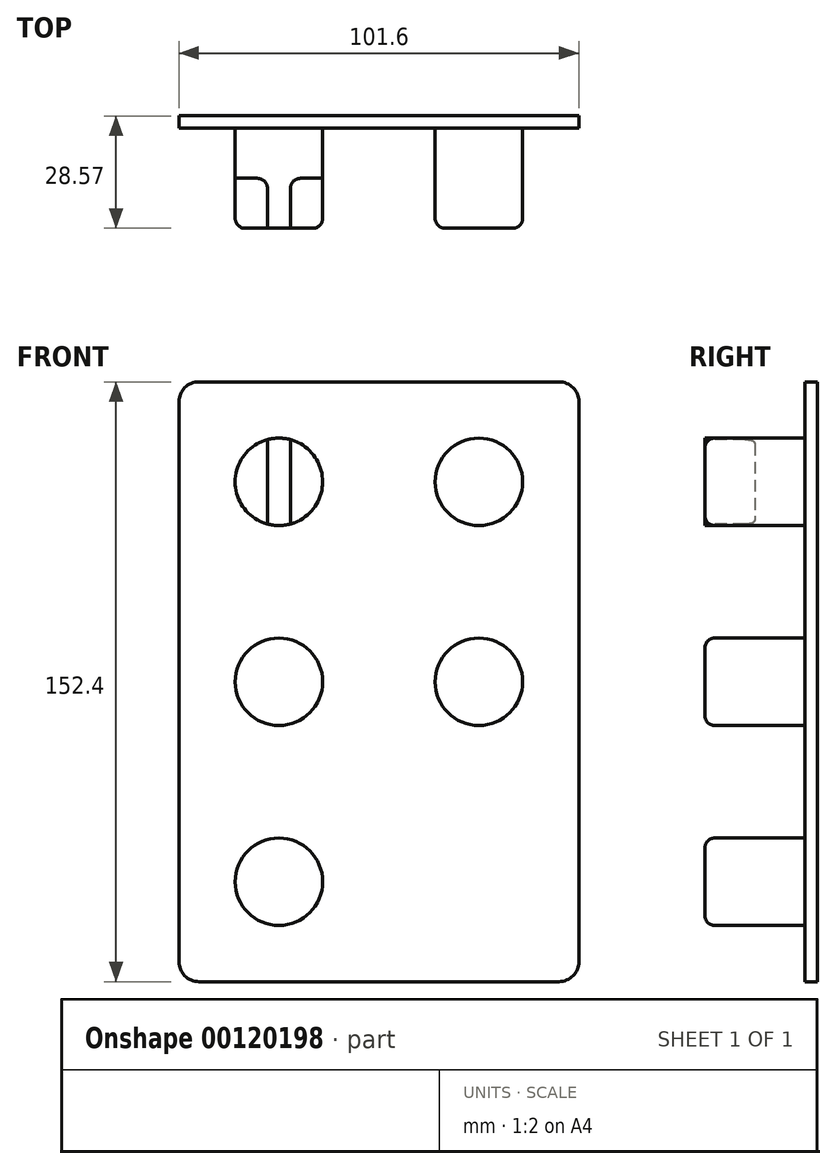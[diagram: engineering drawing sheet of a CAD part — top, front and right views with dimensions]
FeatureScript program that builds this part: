
annotation { "Feature Type Name" : "Feature", "Feature Type Description" : "" }
export const myFeature = defineFeature(function(context is Context, id is Id, definition is map)
    precondition{}
    {
        {
            var Q0;
            Q0=qCreatedBy(makeId("Front.planeOp"),FACE);
            var sketch = newSketch(context, id + "F0", { "sketchPlane" : qUnion([Q0])});
            skCircle(sketch, "E0", {"center": v(0, 0) * mm, "radius": 11.11 * mm});
            skCircle(sketch, "E1", {"center": v(0, 50.8) * mm, "radius": 11.11 * mm});
            skCircle(sketch, "E2", {"center": v(0, -50.8) * mm, "radius": 11.11 * mm});
            skCircle(sketch, "E3", {"center": v(50.8, 0) * mm, "radius": 11.11 * mm});
            skCircle(sketch, "E4", {"center": v(50.8, 50.8) * mm, "radius": 11.11 * mm});
            skSolve(sketch);
        }
        {
            var Q0;
            Q0 = qSketchRegion(id + "F0", true);
            extrude(context, id + "F1", {"entities" : qUnion([Q0]), "depth" : 25.4 * mm});
        }
        {
            var Q0;
            Q0=makeQuery(id+"F1.opExtrude","CAP_FACE",FACE,{"disambiguationData":[OSD([sQuery(id+"F0.wireOp",EDGE,"E1")])],"isStart":false});
            var sketch = newSketch(context, id + "F2", { "sketchPlane" : qUnion([Q0])});
            skLineSegment(sketch, "E5.bottom", {"start": v(2.9, 64.23) * mm, "end": v(-2.9, 64.23) * mm});
            skLineSegment(sketch, "E5.top", {"start": v(2.9, 37.37) * mm, "end": v(-2.9, 37.37) * mm});
            skLineSegment(sketch, "E5.left", {"start": v(2.9, 64.23) * mm, "end": v(2.9, 37.37) * mm});
            skLineSegment(sketch, "E5.right", {"start": v(-2.9, 64.23) * mm, "end": v(-2.9, 37.37) * mm});
            skPoint(sketch, "E5.middle", {"position": v(0, 50.8) * mm});
            skSolve(sketch);
        }
        {
            var Q0;
            {var subQ0=sQuery(id+"F2.wireOp",EDGE,"E5.right");var subQ1=makeQuery(id+"F1.opExtrude","CAP_EDGE",EDGE,{"disambiguationData":[OSD([sQuery(id+"F0.wireOp",EDGE,"E1")])],"isStart":false});var subQ2=makeQuery(id+"F2.imprint","INTERSECT",VERTEX,{"disambiguationData":[OD(0.0)],"derivedFrom":[subQ1,subQ0]});Q0=makeQuery(id+"F2.imprint","IMPRINT",FACE,{"disambiguationData":[TD([[makeQuery(id+"F2.imprint","IMPRINT",EDGE,{"disambiguationData":[TD([[subQ2,-1.0]])],"derivedFrom":subQ0}),-1.0]])]});}
            var Q1;
            {var subQ0=sQuery(id+"F2.wireOp",EDGE,"E5.left");var subQ1=makeQuery(id+"F1.opExtrude","CAP_EDGE",EDGE,{"disambiguationData":[OSD([sQuery(id+"F0.wireOp",EDGE,"E1")])],"isStart":false});var subQ2=makeQuery(id+"F2.imprint","INTERSECT",VERTEX,{"disambiguationData":[OD(0.0)],"derivedFrom":[subQ1,subQ0]});Q1=makeQuery(id+"F2.imprint","IMPRINT",FACE,{"disambiguationData":[TD([[makeQuery(id+"F2.imprint","IMPRINT",EDGE,{"disambiguationData":[TD([[subQ2,-1.0]])],"derivedFrom":subQ0}),1.0]])]});}
            extrude(context, id + "F3", {"entities" : qUnion([Q0, Q1]), "operationType" : NewBodyOperationType.REMOVE, "oppositeDirection" : true, "depth" : 12.7 * mm});
        }
        {
            var Q0;
            Q0=makeQuery(id+"F3.boolean.opBoolean","COPY",EDGE,{"derivedFrom":makeQuery(id+"F3.opExtrude","CAP_EDGE",EDGE,{"disambiguationData":[OSD([sQuery(id+"F2.wireOp",EDGE,"E5.right")])],"isStart":true})});
            var Q1;
            Q1=makeQuery(id+"F3.boolean.opBoolean","COPY",EDGE,{"derivedFrom":makeQuery(id+"F3.opExtrude","CAP_EDGE",EDGE,{"disambiguationData":[OSD([sQuery(id+"F2.wireOp",EDGE,"E5.left")])],"isStart":true})});
            var Q2;
            Q2=makeQuery(id+"F3.boolean.opBoolean","COPY",EDGE,{"derivedFrom":makeQuery(id+"F3.opExtrude","CAP_EDGE",EDGE,{"disambiguationData":[OSD([sQuery(id+"F2.wireOp",EDGE,"E5.right")])],"isStart":false})});
            var Q3;
            {var subQ0=sQuery(id+"F2.wireOp",EDGE,"E5.right");var subQ1=sQuery(id+"F0.wireOp",EDGE,"E1");var subQ2=makeQuery(id+"F1.opExtrude","CAP_EDGE",EDGE,{"disambiguationData":[OSD([subQ1])],"isStart":false});Q3=makeQuery(id+"F3.boolean.opBoolean","COPY",EDGE,{"derivedFrom":makeQuery(id+"F3.opExtrude","CAP_EDGE",EDGE,{"disambiguationData":[OSD([subQ1]),TDD([makeQuery(id+"F2.imprint","IMPRINT",EDGE,{"disambiguationData":[TD([[makeQuery(id+"F2.imprint","INTERSECT",VERTEX,{"disambiguationData":[OD(0.0)],"derivedFrom":[subQ2,subQ0]}),-1.0]])],"derivedFrom":subQ2})])],"isStart":false})});}
            var Q4;
            Q4=makeQuery(id+"F3.boolean.opBoolean","COPY",EDGE,{"derivedFrom":makeQuery(id+"F3.opExtrude","CAP_EDGE",EDGE,{"disambiguationData":[OSD([sQuery(id+"F2.wireOp",EDGE,"E5.left")])],"isStart":false})});
            var Q5;
            {var subQ0=sQuery(id+"F2.wireOp",EDGE,"E5.left");var subQ1=sQuery(id+"F0.wireOp",EDGE,"E1");var subQ2=makeQuery(id+"F1.opExtrude","CAP_EDGE",EDGE,{"disambiguationData":[OSD([subQ1])],"isStart":false});Q5=makeQuery(id+"F3.boolean.opBoolean","COPY",EDGE,{"derivedFrom":makeQuery(id+"F3.opExtrude","CAP_EDGE",EDGE,{"disambiguationData":[OSD([subQ1]),TDD([makeQuery(id+"F2.imprint","IMPRINT",EDGE,{"disambiguationData":[TD([[makeQuery(id+"F2.imprint","INTERSECT",VERTEX,{"disambiguationData":[OD(0.0)],"derivedFrom":[subQ2,subQ0]}),1.0]])],"derivedFrom":subQ2})])],"isStart":false})});}
            var Q6;
            Q6=makeQuery(id+"F1.opExtrude","CAP_EDGE",EDGE,{"disambiguationData":[OSD([sQuery(id+"F0.wireOp",EDGE,"E4")])],"isStart":false});
            var Q7;
            Q7=makeQuery(id+"F1.opExtrude","CAP_EDGE",EDGE,{"disambiguationData":[OSD([sQuery(id+"F0.wireOp",EDGE,"E3")])],"isStart":false});
            var Q8;
            Q8=makeQuery(id+"F1.opExtrude","CAP_EDGE",EDGE,{"disambiguationData":[OSD([sQuery(id+"F0.wireOp",EDGE,"E0")])],"isStart":false});
            var Q9;
            Q9=makeQuery(id+"F1.opExtrude","CAP_EDGE",EDGE,{"disambiguationData":[OSD([sQuery(id+"F0.wireOp",EDGE,"E2")])],"isStart":false});
            fillet(context, id + "F4", {"entities" : qUnion([Q0, Q1, Q2, Q3, Q4, Q5, Q6, Q7, Q8, Q9]), "radius" : 2.54 * mm, "tangentPropagation" : true, "allowEdgeOverflow" : false});
        }
        {
            var Q0;
            Q0=qCreatedBy(makeId("Front.planeOp"),FACE);
            var sketch = newSketch(context, id + "F5", { "sketchPlane" : qUnion([Q0])});
            skLineSegment(sketch, "E6.bottom", {"start": v(76.2, 76.21) * mm, "end": v(-25.4, 76.21) * mm});
            skLineSegment(sketch, "E6.top", {"start": v(76.2, -76.19) * mm, "end": v(-25.4, -76.19) * mm});
            skLineSegment(sketch, "E6.left", {"start": v(76.2, 76.21) * mm, "end": v(76.2, -76.19) * mm});
            skLineSegment(sketch, "E6.right", {"start": v(-25.4, 76.21) * mm, "end": v(-25.4, -76.19) * mm});
            skSolve(sketch);
        }
        {
            var Q0;
            Q0 = qSketchRegion(id + "F5", true);
            extrude(context, id + "F6", {"entities" : qUnion([Q0]), "oppositeDirection" : true, "depth" : 3.17 * mm});
        }
        {
            var Q0;
            Q0=makeQuery(id+"F6.opExtrude","SWEPT_EDGE",EDGE,{"disambiguationData":[OSD([sQuery(id+"F5.wireOp",EDGE,"E6.bottom"),sQuery(id+"F5.wireOp",EDGE,"E6.right")])]});
            var Q1;
            Q1=makeQuery(id+"F6.opExtrude","SWEPT_EDGE",EDGE,{"disambiguationData":[OSD([sQuery(id+"F5.wireOp",EDGE,"E6.bottom"),sQuery(id+"F5.wireOp",EDGE,"E6.left")])]});
            var Q2;
            Q2=makeQuery(id+"F6.opExtrude","SWEPT_EDGE",EDGE,{"disambiguationData":[OSD([sQuery(id+"F5.wireOp",EDGE,"E6.top"),sQuery(id+"F5.wireOp",EDGE,"E6.left")])]});
            var Q3;
            Q3=makeQuery(id+"F6.opExtrude","SWEPT_EDGE",EDGE,{"disambiguationData":[OSD([sQuery(id+"F5.wireOp",EDGE,"E6.top"),sQuery(id+"F5.wireOp",EDGE,"E6.right")])]});
            fillet(context, id + "F7", {"entities" : qUnion([Q0, Q1, Q2, Q3]), "radius" : 5.08 * mm, "tangentPropagation" : true, "allowEdgeOverflow" : false});
        }
    });
